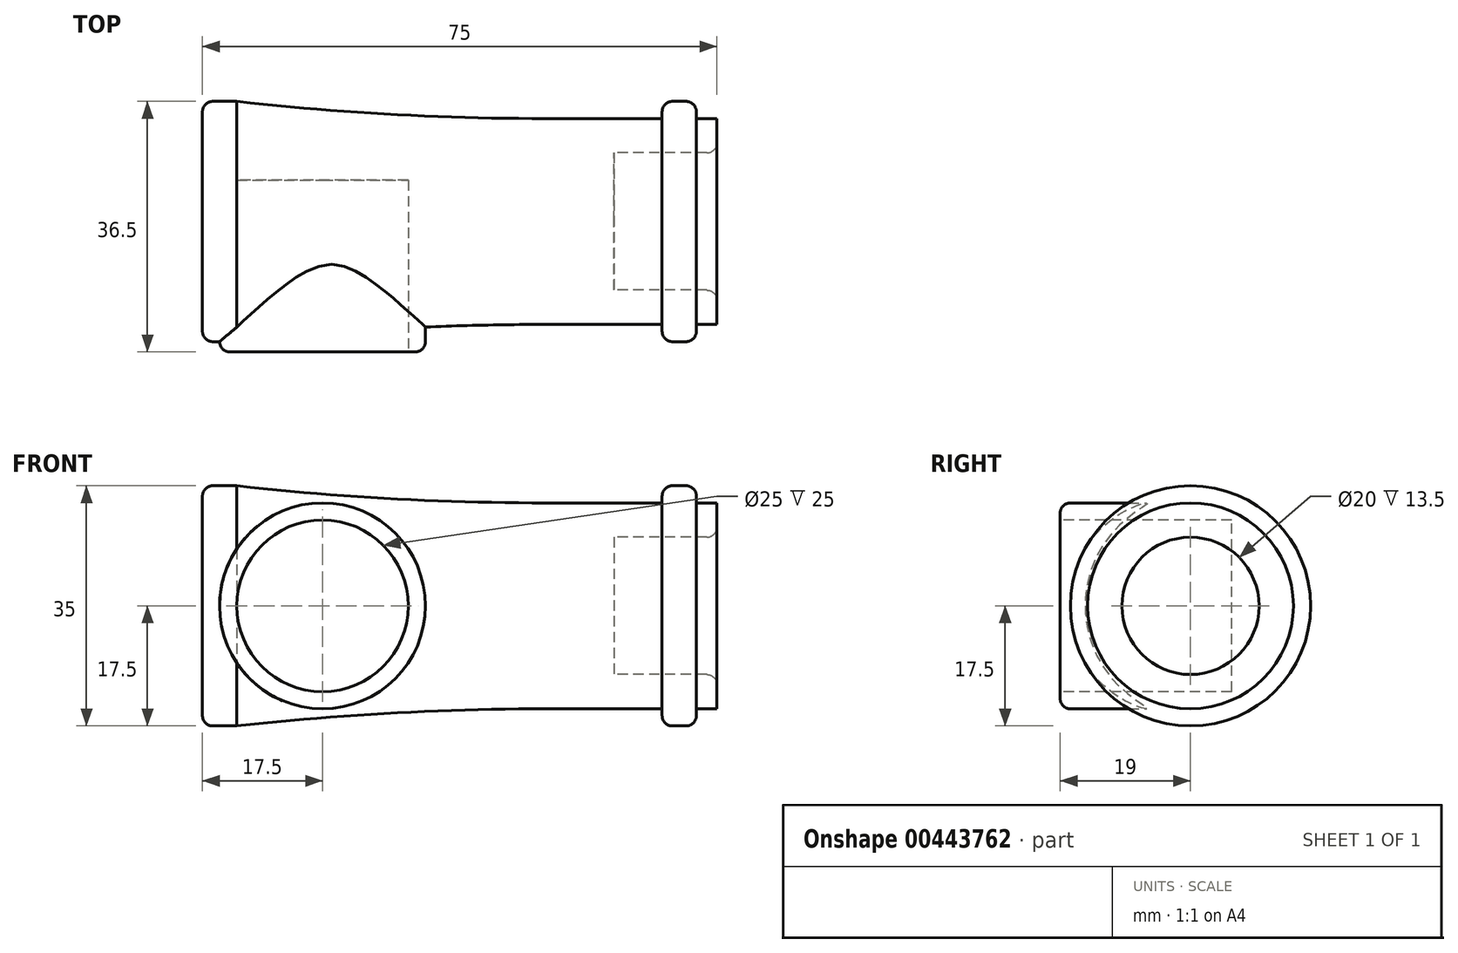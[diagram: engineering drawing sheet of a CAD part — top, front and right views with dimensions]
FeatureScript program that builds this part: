
annotation { "Feature Type Name" : "Feature", "Feature Type Description" : "" }
export const myFeature = defineFeature(function(context is Context, id is Id, definition is map)
    precondition{}
    {
        {
            var Q0;
            Q0=qCreatedBy(makeId("Front.planeOp"),FACE);
            var sketch = newSketch(context, id + "F0", { "sketchPlane" : qUnion([Q0])});
            skLineSegment(sketch, "E0", {"start": v(0, 0) * mm, "end": v(0, 17.5) * mm});
            skLineSegment(sketch, "E1", {"start": v(0, 0) * mm, "end": v(60, 0) * mm});
            skLineSegment(sketch, "E2", {"start": v(60, 0) * mm, "end": v(60, 10) * mm});
            skLineSegment(sketch, "E3", {"start": v(60, 10) * mm, "end": v(75, 10) * mm});
            skLineSegment(sketch, "E4", {"start": v(75, 10) * mm, "end": v(75, 15) * mm});
            skLineSegment(sketch, "E5", {"start": v(75, 15) * mm, "end": v(72, 15) * mm});
            skLineSegment(sketch, "E6", {"start": v(72, 15) * mm, "end": v(72, 17.5) * mm});
            skLineSegment(sketch, "E7", {"start": v(72, 17.5) * mm, "end": v(67, 17.5) * mm});
            skLineSegment(sketch, "E8", {"start": v(67, 17.5) * mm, "end": v(67, 15) * mm});
            skLineSegment(sketch, "E9", {"start": v(67, 15) * mm, "end": v(50, 15) * mm});
            skLineSegment(sketch, "E10", {"start": v(0, 17.5) * mm, "end": v(5, 17.5) * mm});
            skArc(sketch, "E11", {"start": v(5, 17.5) * mm, "mid": v(27.47, 15.63) * mm, "end": v(50, 15) * mm});
            skSolve(sketch);
        }
        {
            var Q0;
            Q0 = qSketchRegion(id + "F0", true);
            var Q1;
            Q1=sQuery(id+"F0.wireOp",EDGE,"E1");
            revolve(context, id + "F1", {"entities" : qUnion([Q0]), "axis" : qUnion([Q1]), "revolveType" : RevolveType.FULL});
        }
        {
            var Q0;
            Q0=qCreatedBy(makeId("Front.planeOp"),FACE);
            var sketch = newSketch(context, id + "F2", { "sketchPlane" : qUnion([Q0])});
            skCircle(sketch, "E12", {"center": v(17.5, 0) * mm, "radius": 15 * mm});
            skSolve(sketch);
        }
        {
            var Q0;
            Q0 = qSketchRegion(id + "F2", true);
            extrude(context, id + "F3", {"entities" : qUnion([Q0]), "operationType" : NewBodyOperationType.ADD, "depth" : 19 * mm});
        }
        {
            var Q0;
            Q0=makeQuery(id+"F3.opExtrude","CAP_FACE",FACE,{"disambiguationData":[OSD([sQuery(id+"F2.wireOp",EDGE,"E12")])],"isStart":false});
            var sketch = newSketch(context, id + "F4", { "sketchPlane" : qUnion([Q0])});
            skCircle(sketch, "E13", {"center": v(17.5, 0) * mm, "radius": 12.5 * mm});
            skSolve(sketch);
        }
        {
            var Q0;
            Q0 = qSketchRegion(id + "F4", true);
            extrude(context, id + "F5", {"entities" : qUnion([Q0]), "operationType" : NewBodyOperationType.REMOVE, "oppositeDirection" : true, "depth" : 25 * mm});
        }
        {
            var Q0;
            Q0=makeQuery(id+"F1.opRevolve","SWEPT_EDGE",EDGE,{"disambiguationData":[OSD([sQuery(id+"F0.wireOp",EDGE,"E0"),sQuery(id+"F0.wireOp",EDGE,"E10")])]});
            var Q1;
            Q1=makeQuery(id+"F3.opExtrude","CAP_EDGE",EDGE,{"disambiguationData":[OSD([sQuery(id+"F2.wireOp",EDGE,"E12")])],"isStart":false});
            var Q2;
            Q2=makeQuery(id+"F1.opRevolve","SWEPT_FACE",FACE,{"disambiguationData":[OSD([sQuery(id+"F0.wireOp",EDGE,"E7")])]});
            var Q3;
            Q3=makeQuery(id+"F1.opRevolve","SWEPT_EDGE",EDGE,{"disambiguationData":[OSD([sQuery(id+"F0.wireOp",EDGE,"E6"),sQuery(id+"F0.wireOp",EDGE,"E7")])]});
            var Q4;
            Q4=makeQuery(id+"F1.opRevolve","SWEPT_EDGE",EDGE,{"disambiguationData":[OSD([sQuery(id+"F0.wireOp",EDGE,"E3"),sQuery(id+"F0.wireOp",EDGE,"E4")])]});
            fillet(context, id + "F6", {"entities" : qUnion([Q0, Q1, Q2, Q3, Q4]), "radius" : 1.5 * mm, "tangentPropagation" : true, "allowEdgeOverflow" : false});
        }
    });
